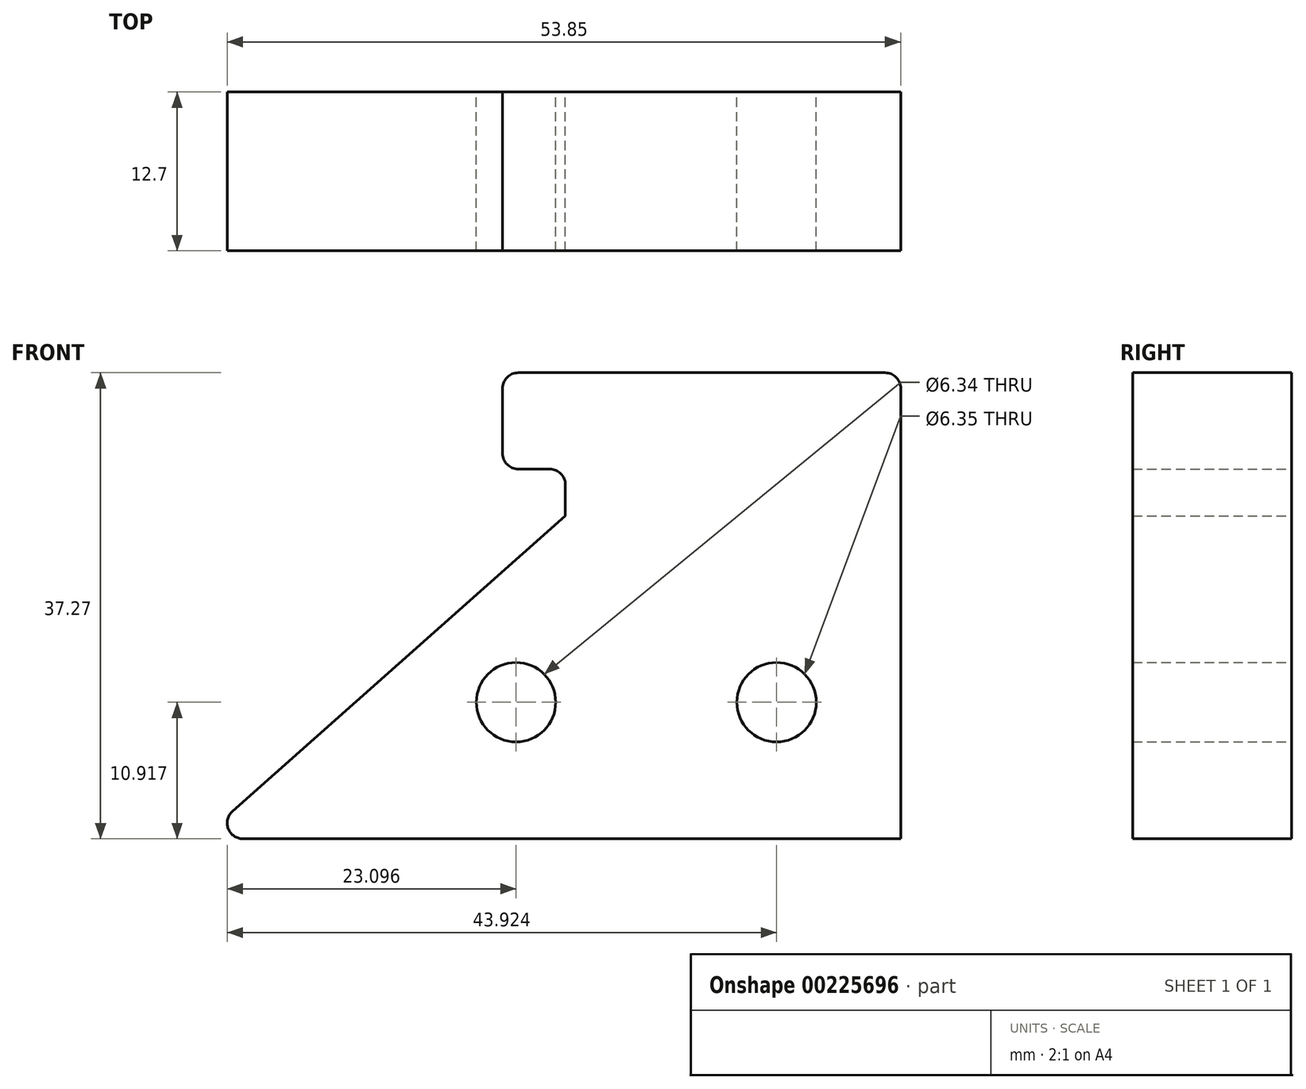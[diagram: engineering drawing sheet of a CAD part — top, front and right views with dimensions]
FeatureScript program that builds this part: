
annotation { "Feature Type Name" : "Feature", "Feature Type Description" : "" }
export const myFeature = defineFeature(function(context is Context, id is Id, definition is map)
    precondition{}
    {
        {
            var Q0;
            Q0=qCreatedBy(makeId("Front.planeOp"),FACE);
            var sketch = newSketch(context, id + "F0", { "sketchPlane" : qUnion([Q0])});
            skLineSegment(sketch, "E0.top", {"start": v(-13.23, -25.81) * mm, "end": v(39.36, -25.81) * mm});
            skLineSegment(sketch, "E0.right", {"start": v(39.36, 10.2) * mm, "end": v(39.36, -25.81) * mm});
            skLineSegment(sketch, "E1", {"start": v(-14.06, -23.61) * mm, "end": v(12.55, 0) * mm});
            skLineSegment(sketch, "E2", {"start": v(12.55, 0) * mm, "end": v(12.55, 2.5) * mm});
            skLineSegment(sketch, "E3", {"start": v(11.3, 3.75) * mm, "end": v(8.79, 3.75) * mm});
            skLineSegment(sketch, "E4", {"start": v(7.53, 5.01) * mm, "end": v(7.53, 10.2) * mm});
            skLineSegment(sketch, "E5", {"start": v(8.79, 11.46) * mm, "end": v(38.1, 11.46) * mm});
            skPoint(sketch, "E6.visualSharp", {"position": v(7.53, 3.75) * mm});
            skArc(sketch, "E6.filletArc", {"start": v(7.53, 5.01) * mm, "mid": v(7.9, 4.12) * mm, "end": v(8.79, 3.75) * mm});
            skPoint(sketch, "E7.visualSharp", {"position": v(12.55, 3.75) * mm});
            skArc(sketch, "E7.filletArc", {"start": v(12.55, 2.5) * mm, "mid": v(12.18, 3.38) * mm, "end": v(11.3, 3.75) * mm});
            skArc(sketch, "E8.filletArc", {"start": v(39.36, 10.2) * mm, "mid": v(39, 11.09) * mm, "end": v(38.1, 11.46) * mm});
            skPoint(sketch, "E9.visualSharp", {"position": v(7.53, 11.46) * mm});
            skArc(sketch, "E9.filletArc", {"start": v(8.79, 11.46) * mm, "mid": v(7.9, 11.09) * mm, "end": v(7.53, 10.2) * mm});
            skPoint(sketch, "E10.visualSharp", {"position": v(-16.54, -25.81) * mm});
            skArc(sketch, "E10.filletArc", {"start": v(-14.06, -23.61) * mm, "mid": v(-14.4, -25) * mm, "end": v(-13.23, -25.81) * mm});
            skCircle(sketch, "E11", {"center": v(8.6, -14.9) * mm, "radius": 3.17 * mm});
            skCircle(sketch, "E12", {"center": v(29.43, -14.9) * mm, "radius": 3.18 * mm});
            skSolve(sketch);
        }
        {
            var Q0;
            Q0 = qSketchRegion(id + "F0", true);
            extrude(context, id + "F1", {"entities" : qUnion([Q0]), "depth" : 12.7 * mm});
        }
    });
